# Revit family: NBS_Allermuir_OffcChrs_Famiglia_LoungeChair
name_source: partatom
category: Furniture
revit_build: Autodesk Revit 2016 (Build: 20161004_0715(x64)
units: mm (PartAtom-declared; Revit-internal decimal feet)

## family parameters
Always vertical = Yes
Cut with Voids When Loaded = No
Room Calculation Point = No
Shared = No
Work Plane-Based = No

## types (3) — shared parameters
AssetType = Moveable
Category = Pr_40_50_12_57:Office chairs
DurationUnit = year
EnvironmentalProductDeclaration = http://www.thesenatorgroup.com
ExpectedLife = 5
IfcExportAs = IfcFurnitureType
IfcExportType = CHAIR
IsBuiltIn = No
ManufacturerName = Allermuir
ManufacturerURL = http://www.thesenatorgroup.com
ModelReference = Famiglia lounge
NBSCertification = www.nationalbimlibrary.com/cert/3ppm0vb3
NBSDescription = Office chairs
NBSReference = 45-35-20/330
Name = OfficeChairs_Famiglia_LoungeChair_Allermuir
NominalDepth = 870 mm
NominalHeight = 1075 mm
NominalLength = 840 mm
NominalWidth = 870 mm
ProductInformation = http://www.thesenatorgroup.com
SeatBaseMaterial = NBS_Concept
SeatingSeatMaterial = NBS_Concept
SeatsAndBacksFinish = Fully upholstered
SeatsAndBacksFinishOptions = Decorative railroad stitch detail to perimeter seam, colours: black, white, red, light grey, dark grey and cream, two-tone upholstery
SeatsAndBacksMaterial = Moulded foam
Status = UNSET
Uniclass2015Code = Pr_40_50_12_57
Uniclass2015Title = Office chairs
Uniclass2015Version = Products v1.9
Version = 1
WarrantyDescription = Allermuir warrant that its manufactured products are free from manufacturing defects in materials or workmanship for a period of five years
WarrantyDurationParts = 5
WarrantyDurationUnit = year
zero-valued in all types: HighestSeatingHeight, LowestSeatingHeight

## per-type parameters (varying)
| type | BIMObjectName | Description | Features | FrameColourOptions | FrameFinish | FrameMaterials | OfficeChairBase | SeatingHeight | Size |
| FMG403 | NBS_Allermuir_OfficeChairs_Famiglia_FMG403 | Lounge chair with wood frame | Moulded foam construction, fully upholstered, solid ash frame with a clear finish, solid ssh frame can be stained or colour washed, decorative railroad stitch detail to perimeter seam, colours: black, white, red, light grey, dark grey, and cream, two-tone upholstery | Stained, colour washed | Clear | Solid ash | NBS_Allermuir_OffcChrs_Famiglia_WoodFrame | 370 mm | 840 x 870 x 1075 mm |
| FMG405 | NBS_Allermuir_OfficeChairs_Famiglia_FMG405 | Lounge chair on a 4 star swivel base | Moulded foam construction, fully upholstered, solid ash frame with a clear finish, solid ssh frame can be stained or colour washed, decorative railroad stitch detail to perimeter seam, colours: black, white, red, light grey, dark grey, and cream, two-tone upholstery | Stained, colour washed | Powder coat | Steel | NBS_Allermuir_OffcChrs_Famiglia_4StarSwivelBase | 375 mm | 905 x 900 x 1075 mm |
| FMG408 | NBS_Allermuir_OfficeChairs_Famiglia_FMG408 | Lounge chair on wire frame | Moulded foam construction, fully upholstered, solid ash frame with a clear finish, solid ash frame can be stained or colour washed, decorative railroad stitch detail to perimeter seam, colours: black, white, red, light grey, dark grey, and cream, two-tone upholstery | Chrome, slate grey | Polished Chrome | Tubular steel | NBS_Allermuir_OffcChrs_Famiglia_WireFrame | 375 mm | 840 x 870 x 1075 mm |

note: column(s) folded — value = type name in every type: ModelNumber

## geometry (parser evidence)
native form markers: Sweep x14
no freeform markers — native parametric forms only
